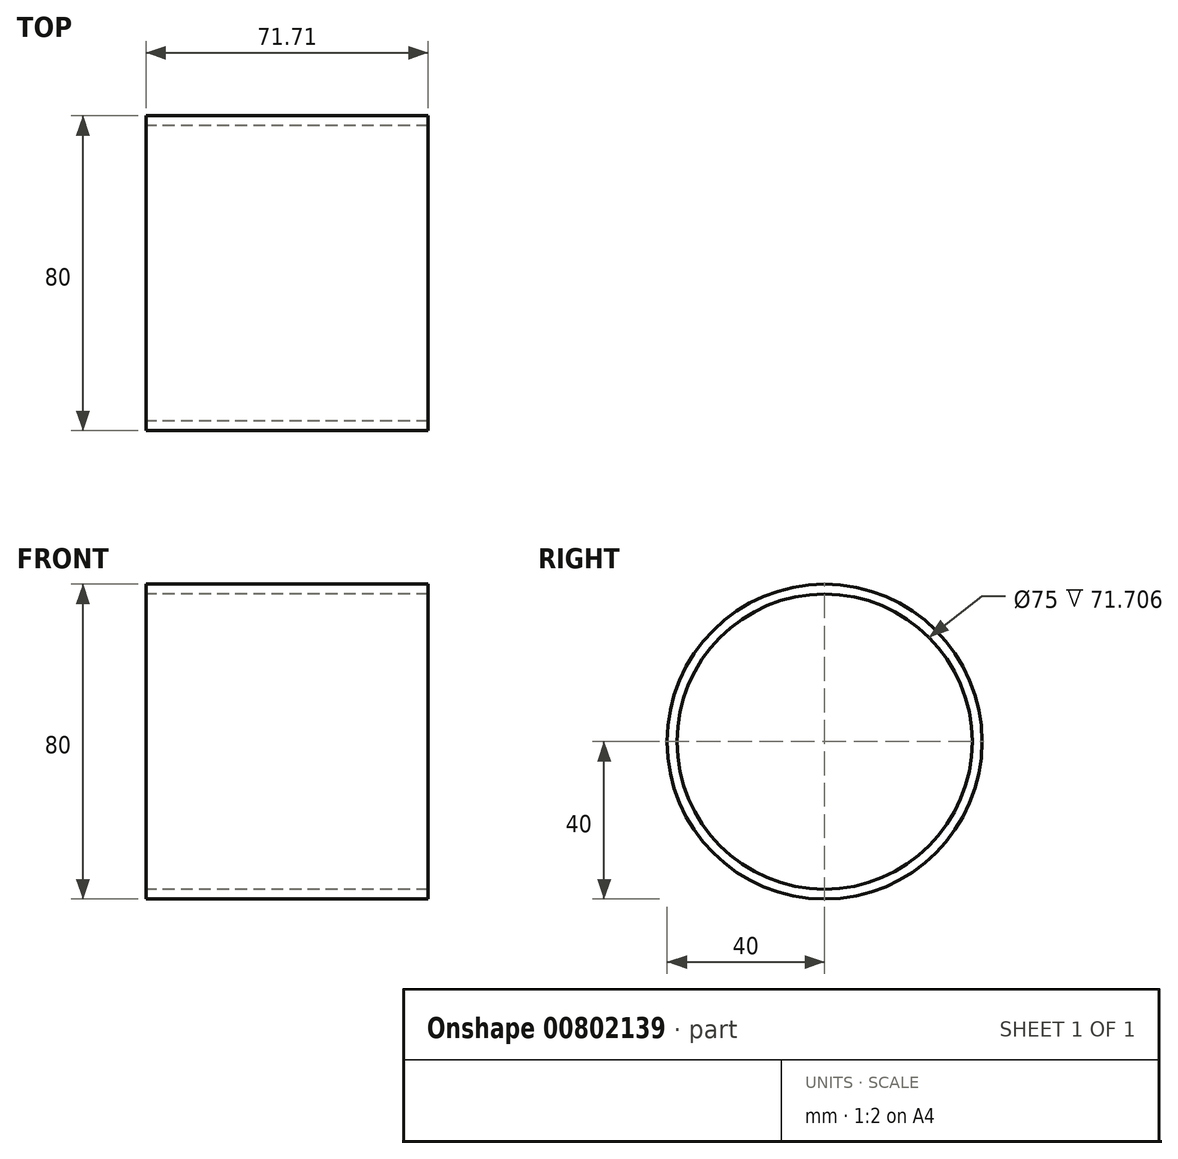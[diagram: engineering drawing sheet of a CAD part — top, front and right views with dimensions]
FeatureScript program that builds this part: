
annotation { "Feature Type Name" : "Feature", "Feature Type Description" : "" }
export const myFeature = defineFeature(function(context is Context, id is Id, definition is map)
    precondition{}
    {
        {
            var Q0;
            Q0=qCreatedBy(makeId("Right.planeOp"),FACE);
            var sketch = newSketch(context, id + "F0", { "sketchPlane" : qUnion([Q0])});
            skCircle(sketch, "E0", {"center": v(0, 0) * mm, "radius": 37.5 * mm});
            skCircle(sketch, "E1", {"center": v(0, 0) * mm, "radius": 40 * mm});
            skSolve(sketch);
        }
        {
            var Q0;
            Q0=qSketchRegion(id+"F0",true);
            extrude(context, id + "F1", {"entities" : qUnion([Q0]), "depth" : 71.7 * mm, "offsetDistance" : 25 * mm});
        }
    });
